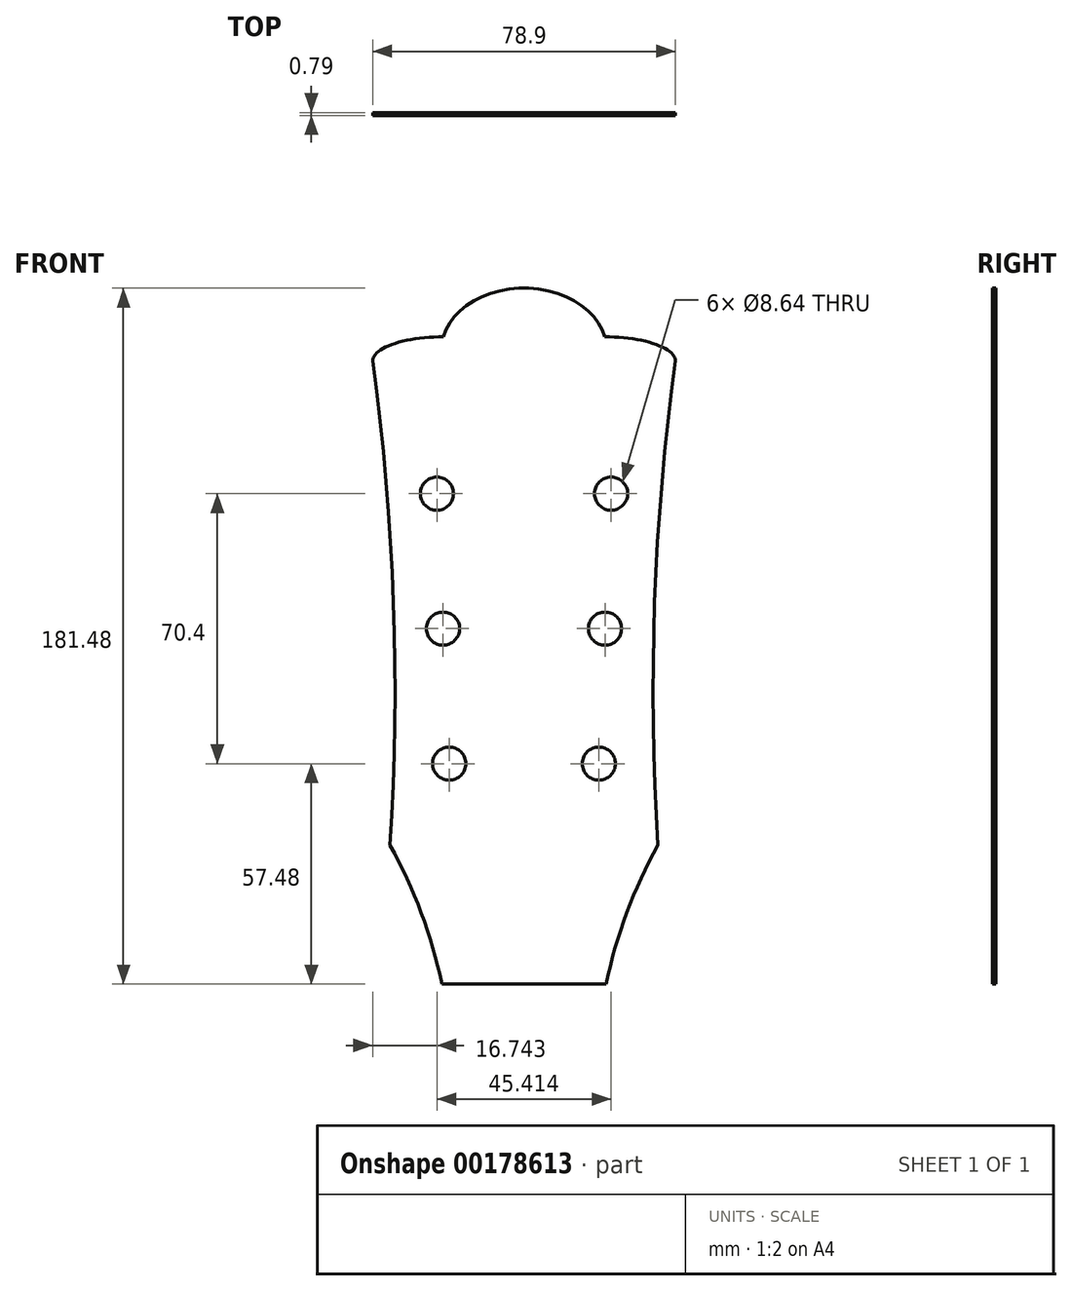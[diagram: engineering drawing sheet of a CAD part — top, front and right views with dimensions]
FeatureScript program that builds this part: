
annotation { "Feature Type Name" : "Feature", "Feature Type Description" : "" }
export const myFeature = defineFeature(function(context is Context, id is Id, definition is map)
    precondition{}
    {
        {
            var Q0;
            Q0=qCreatedBy(makeId("Front.planeOp"),FACE);
            var sketch = newSketch(context, id + "F0", { "sketchPlane" : qUnion([Q0])});
            skPoint(sketch, "E0.middle", {"position": v(130.38, 22.76) * mm});
            skLineSegment(sketch, "E1", {"start": v(130.38, 22.76) * mm, "end": v(130.38, 58.96) * mm, "construction": true});
            skLineSegment(sketch, "E2", {"start": v(130.38, 58.96) * mm, "end": v(130.38, 80.24) * mm, "construction": true});
            skLineSegment(sketch, "E3", {"start": v(130.38, 80.24) * mm, "end": v(130.38, 115.44) * mm, "construction": true});
            skLineSegment(sketch, "E4", {"start": v(130.38, 115.44) * mm, "end": v(130.38, 150.64) * mm, "construction": true});
            skLineSegment(sketch, "E5", {"start": v(130.38, 22.76) * mm, "end": v(108.93, 22.76) * mm, "construction": true});
            skLineSegment(sketch, "E6", {"start": v(130.38, 58.96) * mm, "end": v(95.33, 58.96) * mm, "construction": true});
            skLineSegment(sketch, "E7", {"start": v(130.38, 150.64) * mm, "end": v(130.38, 188.36) * mm, "construction": true});
            skLineSegment(sketch, "E8", {"start": v(130.38, 188.36) * mm, "end": v(90.93, 188.36) * mm, "construction": true});
            skLineSegment(sketch, "E9", {"start": v(130.38, 115.44) * mm, "end": v(97.45, 115.44) * mm, "construction": true});
            skArc(sketch, "E10", {"start": v(95.33, 58.96) * mm, "mid": v(97.23, 123.8) * mm, "end": v(90.93, 188.36) * mm, "construction": true});
            skLineSegment(sketch, "E11", {"start": v(130.38, 188.36) * mm, "end": v(130.38, 196.07) * mm, "construction": true});
            skLineSegment(sketch, "E12", {"start": v(108.93, 22.76) * mm, "end": v(108.17, 31.42) * mm, "construction": true});
            skLineSegment(sketch, "E13", {"start": v(95.33, 58.96) * mm, "end": v(106.76, 47.52) * mm, "construction": true});
            skArc(sketch, "E14", {"start": v(108.17, 31.42) * mm, "mid": v(104.18, 46.32) * mm, "end": v(95.33, 58.96) * mm, "construction": true});
            skArc(sketch, "E15", {"start": v(125.94, 195.83) * mm, "mid": v(116.54, 193.75) * mm, "end": v(107.86, 189.61) * mm, "construction": true});
            skArc(sketch, "E16", {"start": v(90.93, 188.36) * mm, "mid": v(96.84, 187.58) * mm, "end": v(102.8, 187.8) * mm, "construction": true});
            skArc(sketch, "E17", {"start": v(130.38, 191.83) * mm, "mid": v(129.05, 194.82) * mm, "end": v(125.94, 195.83) * mm, "construction": true});
            skArc(sketch, "E18.MirrorCS", {"start": v(169.83, 188.36) * mm, "mid": v(163.92, 187.58) * mm, "end": v(157.97, 187.8) * mm, "construction": true});
            skArc(sketch, "E19.MirrorCS", {"start": v(152.59, 31.42) * mm, "mid": v(156.58, 46.32) * mm, "end": v(165.43, 58.96) * mm, "construction": true});
            skArc(sketch, "E20.MirrorCS", {"start": v(165.43, 58.96) * mm, "mid": v(163.53, 123.8) * mm, "end": v(169.83, 188.36) * mm, "construction": true});
            skLineSegment(sketch, "E21.MirrorCS", {"start": v(165.43, 58.96) * mm, "end": v(154, 47.52) * mm, "construction": true});
            skLineSegment(sketch, "E22.MirrorCS", {"start": v(151.83, 22.76) * mm, "end": v(152.59, 31.42) * mm, "construction": true});
            skArc(sketch, "E23.MirrorCS", {"start": v(134.82, 195.83) * mm, "mid": v(144.21, 193.75) * mm, "end": v(152.9, 189.61) * mm, "construction": true});
            skLineSegment(sketch, "E24.MirrorCS", {"start": v(130.38, 22.76) * mm, "end": v(151.83, 22.76) * mm, "construction": true});
            skArc(sketch, "E25.MirrorCS", {"start": v(130.38, 191.83) * mm, "mid": v(131.7, 194.82) * mm, "end": v(134.82, 195.83) * mm, "construction": true});
            skArc(sketch, "E26", {"start": v(152.9, 189.61) * mm, "mid": v(155.33, 188.43) * mm, "end": v(157.97, 187.8) * mm, "construction": true});
            skLineSegment(sketch, "E27.direction1", {"start": v(130.38, 22.76) * mm, "end": v(180.38, 22.76) * mm, "construction": true});
            skArc(sketch, "E28.MirrorC", {"start": v(107.86, 189.61) * mm, "mid": v(105.42, 188.43) * mm, "end": v(102.8, 187.8) * mm, "construction": true});
            skPoint(sketch, "E29.orphan", {"position": v(154.79, 188.36) * mm});
            skPoint(sketch, "E30.orphan", {"position": v(105.97, 188.36) * mm});
            skLineSegment(sketch, "E31", {"start": v(-21.43, 0) * mm, "end": v(21.43, 0) * mm});
            skLineSegment(sketch, "E32", {"start": v(0, 0) * mm, "end": v(0, 165.6) * mm, "construction": true});
            skLineSegment(sketch, "E33", {"start": v(0, 165.6) * mm, "end": v(-39.45, 165.6) * mm, "construction": true});
            skPoint(sketch, "E34", {"position": v(0, 36.2) * mm});
            skLineSegment(sketch, "E35", {"start": v(0, 36.2) * mm, "end": v(-34.93, 36.2) * mm, "construction": true});
            skArc(sketch, "E36", {"start": v(-21.43, 0) * mm, "mid": v(-26.8, 18.61) * mm, "end": v(-34.92, 36.2) * mm});
            skEllipse(sketch, "E37", {"center": v(0, 165.6) * mm, "majorRadius": 21.43 * mm, "minorRadius": 15.88 * mm, "majorAxis": v(1, 0)});
            skLineSegment(sketch, "E38", {"start": v(21.43, 0) * mm, "end": v(21.43, 206.05) * mm, "construction": true});
            skLineSegment(sketch, "E39", {"start": v(-39.45, 165.6) * mm, "end": v(-39.45, 162.43) * mm, "construction": true});
            skArc(sketch, "E40", {"start": v(-34.92, 36.2) * mm, "mid": v(-34.04, 99.43) * mm, "end": v(-39.45, 162.43) * mm});
            skEllipse(sketch, "E41", {"center": v(-21, 162.43) * mm, "majorRadius": 18.45 * mm, "minorRadius": 6.35 * mm, "majorAxis": v(-1, 0)});
            skEllipse(sketch, "E42.MirrorC", {"center": v(21, 162.43) * mm, "majorRadius": 18.45 * mm, "minorRadius": 6.35 * mm, "majorAxis": v(1, 0)});
            skArc(sketch, "E43.MirrorCS", {"start": v(21.43, 0) * mm, "mid": v(26.8, 18.61) * mm, "end": v(34.92, 36.2) * mm});
            skArc(sketch, "E44.MirrorCS", {"start": v(34.92, 36.2) * mm, "mid": v(34.04, 99.43) * mm, "end": v(39.45, 162.43) * mm});
            skSolve(sketch);
        }
        {
            var Q0;
            Q0=makeQuery(id+"F0.imprint","IMPRINT",FACE,{"disambiguationData":[TD([[makeQuery(id+"F0.imprint","IMPRINT",EDGE,{"derivedFrom":sQuery(id+"F0.wireOp",EDGE,"E31")}),1.0]])]});
            var Q1;
            {var subQ0=sQuery(id+"F0.wireOp",EDGE,"E41");var subQ1=sQuery(id+"F0.wireOp",EDGE,"E37");var subQ2=makeQuery(id+"F0.imprint","INTERSECT",VERTEX,{"disambiguationData":[OD(0.0)],"derivedFrom":[subQ1,subQ0]});Q1=makeQuery(id+"F0.imprint","IMPRINT",FACE,{"disambiguationData":[TD([[makeQuery(id+"F0.imprint","IMPRINT",EDGE,{"disambiguationData":[TD([[subQ2,-1.0]])],"derivedFrom":subQ1}),-1.0]])]});}
            var Q2;
            {var subQ0=sQuery(id+"F0.wireOp",EDGE,"E41");var subQ1=sQuery(id+"F0.wireOp",EDGE,"E37");var subQ2=makeQuery(id+"F0.imprint","INTERSECT",VERTEX,{"disambiguationData":[OD(0.0)],"derivedFrom":[subQ1,subQ0]});Q2=makeQuery(id+"F0.imprint","IMPRINT",FACE,{"disambiguationData":[TD([[makeQuery(id+"F0.imprint","IMPRINT",EDGE,{"disambiguationData":[TD([[subQ2,-1.0]])],"derivedFrom":subQ1}),1.0]])]});}
            var Q3;
            {var subQ0=sQuery(id+"F0.wireOp",EDGE,"E41");var subQ1=sQuery(id+"F0.wireOp",EDGE,"E37");var subQ2=makeQuery(id+"F0.imprint","INTERSECT",VERTEX,{"disambiguationData":[OD(0.0)],"derivedFrom":[subQ1,subQ0]});Q3=makeQuery(id+"F0.imprint","IMPRINT",FACE,{"disambiguationData":[TD([[makeQuery(id+"F0.imprint","IMPRINT",EDGE,{"disambiguationData":[TD([[subQ2,1.0]])],"derivedFrom":subQ1}),1.0]])]});}
            var Q4;
            {var subQ0=sQuery(id+"F0.wireOp",EDGE,"E42.MirrorC");var subQ1=sQuery(id+"F0.wireOp",EDGE,"E37");var subQ2=makeQuery(id+"F0.imprint","INTERSECT",VERTEX,{"disambiguationData":[OD(0.0)],"derivedFrom":[subQ1,subQ0]});Q4=makeQuery(id+"F0.imprint","IMPRINT",FACE,{"disambiguationData":[TD([[makeQuery(id+"F0.imprint","IMPRINT",EDGE,{"disambiguationData":[TD([[subQ2,1.0]])],"derivedFrom":subQ1}),1.0]])]});}
            var Q5;
            {var subQ0=sQuery(id+"F0.wireOp",EDGE,"E42.MirrorC");var subQ1=sQuery(id+"F0.wireOp",EDGE,"E37");var subQ2=makeQuery(id+"F0.imprint","INTERSECT",VERTEX,{"disambiguationData":[OD(0.0)],"derivedFrom":[subQ1,subQ0]});Q5=makeQuery(id+"F0.imprint","IMPRINT",FACE,{"disambiguationData":[TD([[makeQuery(id+"F0.imprint","IMPRINT",EDGE,{"disambiguationData":[TD([[subQ2,1.0]])],"derivedFrom":subQ1}),-1.0]])]});}
            extrude(context, id + "F1", {"entities" : qUnion([Q0, Q1, Q2, Q3, Q4, Q5]), "depth" : 0.8 * mm});
        }
        {
            var Q0;
            Q0=makeQuery(id+"F1.opExtrude","CAP_FACE",FACE,{"disambiguationData":[OSD([sQuery(id+"F0.wireOp",EDGE,"E31"),sQuery(id+"F0.wireOp",EDGE,"E36"),sQuery(id+"F0.wireOp",EDGE,"E37"),sQuery(id+"F0.wireOp",EDGE,"E40"),sQuery(id+"F0.wireOp",EDGE,"E41"),sQuery(id+"F0.wireOp",EDGE,"E42.MirrorC"),sQuery(id+"F0.wireOp",EDGE,"E43.MirrorCS"),sQuery(id+"F0.wireOp",EDGE,"E44.MirrorCS")])],"isStart":false});
            var sketch = newSketch(context, id + "F2", { "sketchPlane" : qUnion([Q0])});
            skPoint(sketch, "E45", {"position": v(-22.7, 127.88) * mm});
            skPoint(sketch, "E46", {"position": v(-21.1, 92.68) * mm});
            skPoint(sketch, "E47", {"position": v(-19.5, 57.48) * mm});
            skLineSegment(sketch, "E48", {"start": v(0, 0) * mm, "end": v(0, 169.31) * mm, "construction": true});
            skLineSegment(sketch, "E49.MirrorCS", {"start": v(-19.5, 57.48) * mm, "end": v(-22.84, 130.7) * mm, "construction": true});
            skPoint(sketch, "E50.MirrorP", {"position": v(22.7, 127.88) * mm});
            skPoint(sketch, "E51.MirrorP", {"position": v(21.1, 92.68) * mm});
            skPoint(sketch, "E52.MirrorP", {"position": v(19.5, 57.48) * mm});
            skSolve(sketch);
        }
        {
            var Q0;
            Q0=sQuery(id+"F2.wireOp",VERTEX,"E47");
            var Q1;
            Q1=sQuery(id+"F2.wireOp",VERTEX,"E52.MirrorP");
            var Q2;
            Q2=sQuery(id+"F2.wireOp",VERTEX,"E51.MirrorP");
            var Q3;
            Q3=sQuery(id+"F2.wireOp",VERTEX,"E46");
            var Q4;
            Q4=sQuery(id+"F2.wireOp",VERTEX,"E45");
            var Q5;
            Q5=sQuery(id+"F2.wireOp",VERTEX,"E50.MirrorP");
            var Q6;
            Q6=makeQuery(id+"F1.opExtrude","SWEPT_BODY",BODY,{"disambiguationData":[OSD([sQuery(id+"F0.wireOp",EDGE,"E31"),sQuery(id+"F0.wireOp",EDGE,"E36"),sQuery(id+"F0.wireOp",EDGE,"E37"),sQuery(id+"F0.wireOp",EDGE,"E40"),sQuery(id+"F0.wireOp",EDGE,"E41"),sQuery(id+"F0.wireOp",EDGE,"E42.MirrorC"),sQuery(id+"F0.wireOp",EDGE,"E43.MirrorCS"),sQuery(id+"F0.wireOp",EDGE,"E44.MirrorCS")])]});
            hole(context, id + "F3", {"style" : HoleStyle.SIMPLE, "endStyle" : HoleEndStyle.BLIND, "holeDiameter" : 8.64 * mm, "holeDepth" : 19.05 * mm, "locations" : qUnion([Q0, Q1, Q2, Q3, Q4, Q5]), "scope" : qUnion([Q6])});
        }
    });
